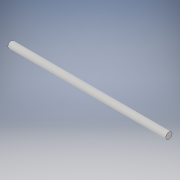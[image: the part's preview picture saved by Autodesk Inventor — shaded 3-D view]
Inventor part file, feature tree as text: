
AUTODESK INVENTOR PART (.ipt)
format: ipt  version: 2019 (Build 230136000, 136)  size: 90,112 bytes
history: native  units: in
note: dims shown in document units (in); Inventor stores cm internally (conversion verified against a paired STEP export)
features: extrude x1, sketch x1
ambient origin geometry x8: Origin, YZ Plane, XZ Plane, XY Plane, X Axis, Y Axis, Z Axis, Center Point
bodies: Solid1 (feature_tree)
feature tree (2):
  extrude  "Extrusion1"  Depth=5.9055in TaperAngle=0.0deg
  sketch  "Sketch1"  dims[d0=0.2362in d1=5.9055in d2=0.0in]
